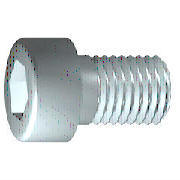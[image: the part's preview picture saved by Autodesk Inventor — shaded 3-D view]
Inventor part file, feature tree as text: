
AUTODESK INVENTOR PART (.ipt)
format: ipt  version: 2025 (Build 290162000, 162)  size: 183,808 bytes
history: native  units: mm (DEFAULTED — no unit token found)
features: extrude x1, plane x1, fillet x1
ambient origin geometry x7: Origin, YZ Plane, XY Plane, X Axis, Y Axis, Z Axis, Center Point
bodies: Solid1 (feature_tree), Body (feature_tree)
feature tree (3):
  extrude  "Slot"  Depth=22.0mm
  plane  "Work Plane1"
  fillet  "Fillet2"  Radius=0.49086mm
